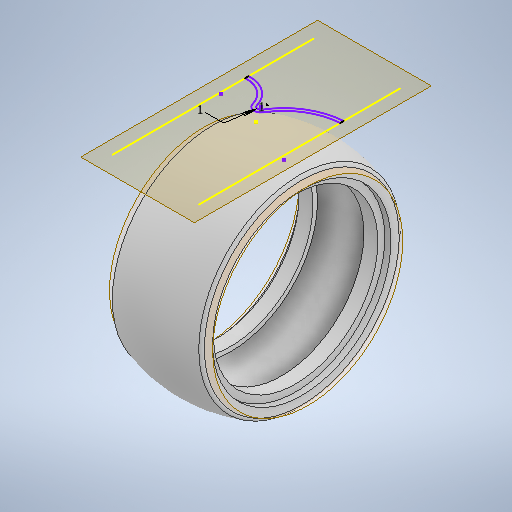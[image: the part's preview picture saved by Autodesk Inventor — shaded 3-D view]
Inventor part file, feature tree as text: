
AUTODESK INVENTOR PART (.ipt)
format: ipt  version: 2025 (Build 290162000, 162)  size: 389,120 bytes
history: native  units: in
note: dims shown in document units (in); Inventor stores cm internally (conversion verified against a paired STEP export)
features: sketch x3, revolve x2, plane x1, other x1
ambient origin geometry x8: Origin, YZ Plane, XZ Plane, XY Plane, X Axis, Y Axis, Z Axis, Center Point
bodies: Solid1 (feature_tree)
feature tree (7):
  revolve  "Revolution1"  [1 undecoded]
  plane  "Work Plane1"
  sketch  "Sketch3"  dims[d4=0.0799in d5=0.0701in d6=0.1232in d7=1.2354in d8=0.0394in d9=0.0394in d10=0.0522in d11=90.0deg d12=0.0276in d13=90.0deg d14=1.4375in d15=0.0394in d16=0.0394in d17=0.0197in d18=0.0344in d19=0.0197in d20=0.0344in]
  sketch  "Sketch1"  dims[d0=1.0449in d1=0.9425in]
  sketch  "Sketch2"  dims[d2=0.2925in d3=0.1598in]
  other  "Srf1"
  revolve  "RevolutionSrf1"  [1 undecoded]
note: 2 required parameter values undecoded (feature->parameter linkage not recoverable at this tier; creation-order binding heuristic only, values carry confidence <= 0.55)
